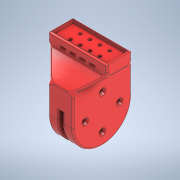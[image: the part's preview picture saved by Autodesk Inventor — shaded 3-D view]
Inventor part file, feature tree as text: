
AUTODESK INVENTOR PART (.ipt)
format: ipt  version: 2022 (Build 260153000, 153)  size: 672,256 bytes
history: native  units: mm
features: sketch x11, extrude x10, other x6, projected_geometry x4, chamfer x2, loft x1, fillet x1
ambient origin geometry x8: Origin, YZ Plane, XZ Plane, XY Plane, X Axis, Y Axis, Z Axis, Center Point
bodies: Body1 (feature_tree)
feature tree (35):
  other  "Твердое тело1"
  extrude  "Выдавливание1"  Depth=20.0mm
  extrude  "Выдавливание2"  Depth=55.6mm
  extrude  "Выдавливание4"  Depth=2.5mm
  extrude  "Выдавливание9"  Depth=2.0mm
  other  "РабПлоскость2"
  extrude  "Выдавливание10"  Depth=2.0mm TaperAngle=0.0deg
  extrude  "Выдавливание11"  Depth=2.0mm
  other  "РабПлоскость3"
  loft  "Лофт1"
  other  "РабПлоскость5"
  sketch  "Эскиз18"
  other  "РабПлоскость6"
  extrude  "Выдавливание14"  Depth=5.0mm TaperAngle=0.0deg
  extrude  "Выдавливание15"  Depth=14.0mm
  other  "РабПлоскость7"
  sketch  "Эскиз20"
  chamfer  "Фаска1"  Distance=40.0mm Angle=360.0deg
  extrude  "Выдавливание17"  Depth=3.2mm
  extrude  "Выдавливание18"  Depth=6.2mm
  chamfer  "Фаска2"  Distance=14.0mm
  fillet  "Сопряжение6"  [1 undecoded]
  sketch  "Эскиз1"
  sketch  "Эскиз2"
  projected_geometry  "Спроецированная петля1"
  sketch  "Эскиз12"
  projected_geometry  "Спроецированная петля4"
  sketch  "Эскиз13"
  sketch  "Эскиз14"
  projected_geometry  "Спроецированная петля5"
  sketch  "Эскиз15"
  sketch  "Эскиз17"
  sketch  "Эскиз19"
  sketch  "Эскиз21"
  projected_geometry  "Спроецированная петля6"
note: 1 required parameter value undecoded (feature->parameter linkage not recoverable at this tier; creation-order binding heuristic only, values carry confidence <= 0.55)
